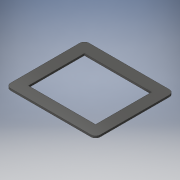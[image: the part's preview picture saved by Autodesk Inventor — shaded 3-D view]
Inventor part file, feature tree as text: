
AUTODESK INVENTOR PART (.ipt)
format: ipt  version: 2016 (Build 200138000, 138)  size: 116,224 bytes
history: native  units: in
note: dims shown in document units (in); Inventor stores cm internally (conversion verified against a paired STEP export)
features: fillet x4, extrude x1, sketch x1
ambient origin geometry x8: Origin, YZ Plane, XZ Plane, XY Plane, X Axis, Y Axis, Z Axis, Center Point
bodies: Solid1 (feature_tree)
feature tree (6):
  extrude  "Extrusion1"  Depth=60.0in
  fillet  "Fillet1"  Radius=12.0in
  fillet  "Fillet2"  Radius=12.0in
  fillet  "Fillet3"  Radius=12.0in
  fillet  "Fillet4"  Radius=12.0in
  sketch  "Sketch1"  dims[d0=72.0in d1=60.0in d2=12.0in d3=12.0in d4=12.0in d5=12.0in d6=2.0in d7=0.0in d8=5.0in d9=5.0in d10=5.0in d11=5.0in]
